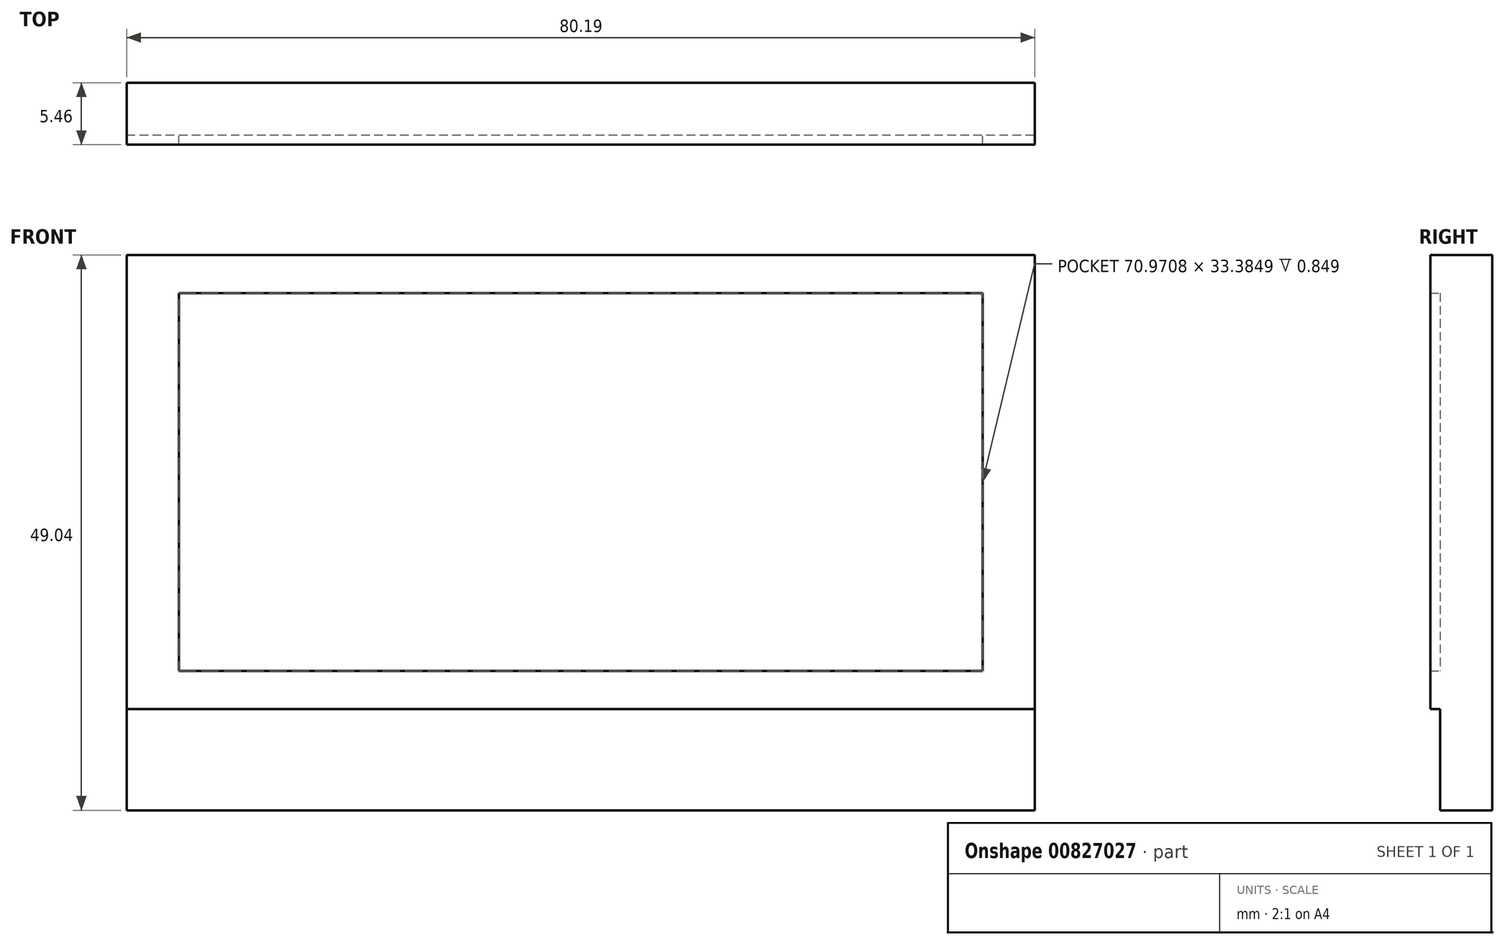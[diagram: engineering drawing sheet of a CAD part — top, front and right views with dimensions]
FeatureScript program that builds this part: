
annotation { "Feature Type Name" : "Feature", "Feature Type Description" : "" }
export const myFeature = defineFeature(function(context is Context, id is Id, definition is map)
    precondition{}
    {
        {
            var Q0;
            Q0=qCreatedBy(makeId("Front.planeOp"),FACE);
            cPlane(context, id + "F0", {"entities" : qUnion([Q0]), "cplaneType" : CPlaneType.OFFSET, "offset" : 8.14 * mm, "width" : 150 * mm, "height" : 150 * mm});
        }
        {
            var Q0;
            Q0=qCreatedBy(makeId("Front.planeOp"),FACE);
            var sketch = newSketch(context, id + "F1", { "sketchPlane" : qUnion([Q0])});
            skLineSegment(sketch, "E0", {"start": v(0, 0) * mm, "end": v(0, 86.64) * mm});
            skLineSegment(sketch, "E1", {"start": v(0, 86.64) * mm, "end": v(141.67, 86.64) * mm});
            skLineSegment(sketch, "E2", {"start": v(0, 0) * mm, "end": v(141.67, 0) * mm});
            skLineSegment(sketch, "E3", {"start": v(141.67, 86.64) * mm, "end": v(141.67, 0) * mm});
            skLineSegment(sketch, "E4", {"start": v(0, 86.64) * mm, "end": v(0, 15.8) * mm});
            skLineSegment(sketch, "E5", {"start": v(141.67, 86.64) * mm, "end": v(141.67, 15.8) * mm});
            skLineSegment(sketch, "E6", {"start": v(0, 15.8) * mm, "end": v(141.67, 15.8) * mm});
            skSolve(sketch);
        }
        {
            var Q0;
            {var subQ2=sQuery(id+"F1.wireOp",EDGE,"E1");Q0=makeQuery(id+"F1.imprint","IMPRINT",FACE,{"disambiguationData":[TD([[makeQuery(id+"F1.imprint","IMPRINT",EDGE,{"derivedFrom":subQ2}),-1.0]])]});}
            var Q1;
            {var subQ2=sQuery(id+"F1.wireOp",EDGE,"E2");Q1=makeQuery(id+"F1.imprint","IMPRINT",FACE,{"disambiguationData":[TD([[makeQuery(id+"F1.imprint","IMPRINT",EDGE,{"derivedFrom":subQ2}),1.0]])]});}
            extrude(context, id + "F2", {"entities" : qUnion([Q0, Q1]), "depth" : 8.14 * mm, "offsetDistance" : 25 * mm});
        }
        {
            var Q0;
            Q0=qCreatedBy(id+"F0.planeOp",FACE);
            var sketch = newSketch(context, id + "F3", { "sketchPlane" : qUnion([Q0])});
            skLineSegment(sketch, "E7", {"start": v(0, 0) * mm, "end": v(0, 15.8) * mm});
            skLineSegment(sketch, "E8", {"start": v(0, 0) * mm, "end": v(141.67, 0) * mm});
            skLineSegment(sketch, "E9", {"start": v(0, 15.8) * mm, "end": v(141.67, 15.8) * mm});
            skLineSegment(sketch, "E10", {"start": v(141.67, 15.8) * mm, "end": v(141.67, 0) * mm});
            skLineSegment(sketch, "E11", {"start": v(0, 15.8) * mm, "end": v(0, 86.63) * mm});
            skLineSegment(sketch, "E12", {"start": v(0, 86.63) * mm, "end": v(141.67, 86.63) * mm});
            skLineSegment(sketch, "E13", {"start": v(141.67, 86.63) * mm, "end": v(141.67, 15.8) * mm});
            skLineSegment(sketch, "E14", {"start": v(0, 86.63) * mm, "end": v(8.14, 86.63) * mm});
            skLineSegment(sketch, "E15.bottom", {"start": v(141.67, 86.63) * mm, "end": v(133.53, 86.63) * mm});
            skLineSegment(sketch, "E15.top", {"start": v(141.67, 86.63) * mm, "end": v(133.53, 86.63) * mm});
            skLineSegment(sketch, "E15.left", {"start": v(141.67, 86.63) * mm, "end": v(141.67, 86.63) * mm});
            skLineSegment(sketch, "E15.right", {"start": v(133.53, 86.63) * mm, "end": v(133.53, 86.63) * mm});
            skLineSegment(sketch, "E16", {"start": v(141.67, 86.63) * mm, "end": v(141.67, 80.7) * mm});
            skLineSegment(sketch, "E17", {"start": v(141.67, 15.8) * mm, "end": v(141.67, 21.72) * mm});
            skLineSegment(sketch, "E18.bottom", {"start": v(8.14, 80.7) * mm, "end": v(133.53, 80.7) * mm});
            skLineSegment(sketch, "E18.top", {"start": v(8.14, 21.72) * mm, "end": v(133.53, 21.72) * mm});
            skLineSegment(sketch, "E18.left", {"start": v(8.14, 80.7) * mm, "end": v(8.14, 21.72) * mm});
            skLineSegment(sketch, "E18.right", {"start": v(133.53, 80.7) * mm, "end": v(133.53, 21.72) * mm});
            skSolve(sketch);
        }
        {
            var Q0;
            Q0=makeQuery(id+"F3.imprint","IMPRINT",FACE,{"disambiguationData":[TD([[makeQuery(id+"F3.imprint","IMPRINT",EDGE,{"derivedFrom":sQuery(id+"F3.wireOp",EDGE,"E9")}),1.0]])]});
            extrude(context, id + "F4", {"entities" : qUnion([Q0]), "operationType" : NewBodyOperationType.ADD, "depth" : 1.5 * mm, "offsetDistance" : 25 * mm});
        }
        {
            var Q0;
            Q0=makeQuery(id+"F2.opExtrude","SWEPT_BODY",BODY,{"disambiguationData":[OSD([sQuery(id+"F1.wireOp",EDGE,"E0"),sQuery(id+"F1.wireOp",EDGE,"E1"),sQuery(id+"F1.wireOp",EDGE,"E2"),sQuery(id+"F1.wireOp",EDGE,"E3")])]});
            var Q1;
            Q1=qCreatedBy(makeId("Origin.pointOp"),VERTEX);
            transform(context, id + "F5", {"entities" : qUnion([Q0]), "transformType" : TransformType.SCALE_UNIFORMLY, "scale" : .566, "scalePoint" : qUnion([Q1]), "makeCopy" : false});
        }
    });
